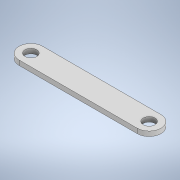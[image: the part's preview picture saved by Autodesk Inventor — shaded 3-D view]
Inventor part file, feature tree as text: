
AUTODESK INVENTOR PART (.ipt)
format: ipt  version: 2020.1 (Build 241239000, 239)  size: 106,496 bytes
history: native  units: in
note: dims shown in document units (in); Inventor stores cm internally (conversion verified against a paired STEP export)
features: extrude x1, sketch x1
ambient origin geometry x8: Origin, YZ Plane, XZ Plane, XY Plane, X Axis, Y Axis, Z Axis, Center Point
bodies: Solid1 (feature_tree)
feature tree (2):
  extrude  "Extrusion1"  Depth=10.0in
  sketch  "Sketch1"  dims[d0=50.0in d1=10.0in d2=5.0in d3=5.0in d4=2.0in d5=0.0in]
